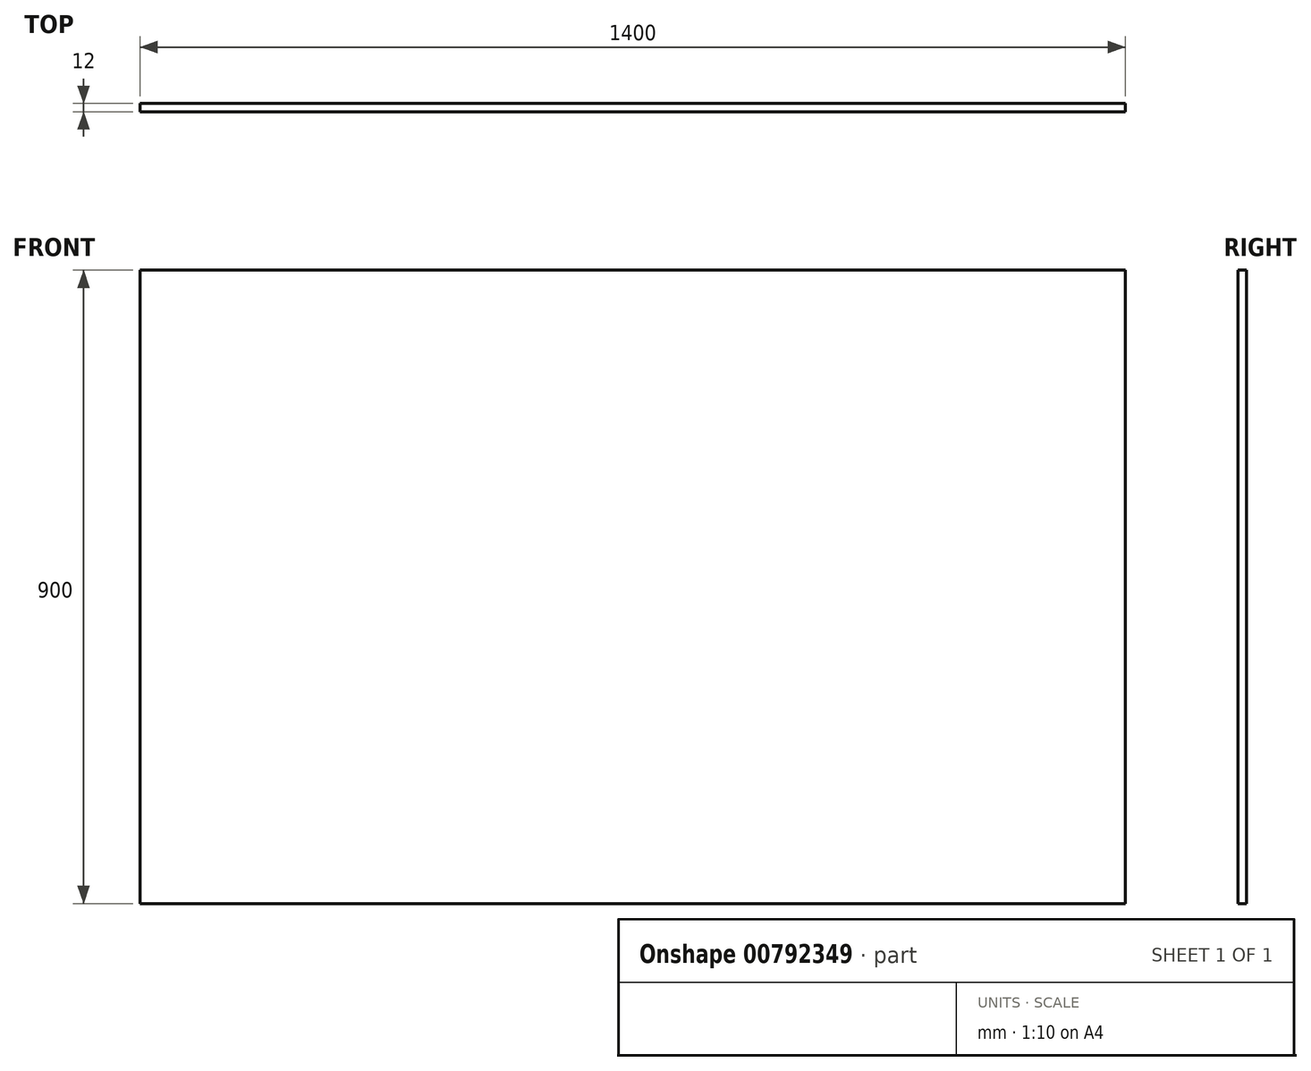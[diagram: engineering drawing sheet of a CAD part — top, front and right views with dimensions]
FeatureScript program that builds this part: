
annotation { "Feature Type Name" : "Feature", "Feature Type Description" : "" }
export const myFeature = defineFeature(function(context is Context, id is Id, definition is map)
    precondition{}
    {
        {
            var Q0;
            Q0=qCreatedBy(makeId("Front.planeOp"),FACE);
            var sketch = newSketch(context, id + "F0", { "sketchPlane" : qUnion([Q0])});
            skLineSegment(sketch, "E0.bottom", {"start": v(-700, 450) * mm, "end": v(700, 450) * mm});
            skLineSegment(sketch, "E0.top", {"start": v(-700, -450) * mm, "end": v(700, -450) * mm});
            skLineSegment(sketch, "E0.left", {"start": v(-700, 450) * mm, "end": v(-700, -450) * mm});
            skLineSegment(sketch, "E0.right", {"start": v(700, 450) * mm, "end": v(700, -450) * mm});
            skLineSegment(sketch, "E1", {"start": v(0, -450) * mm, "end": v(0, 450) * mm, "construction": true});
            skSolve(sketch);
        }
        {
            var Q0;
            Q0 = qSketchRegion(id + "F0", true);
            extrude(context, id + "F1", {"entities" : qUnion([Q0]), "depth" : 12 * mm, "offsetDistance" : 25 * mm});
        }
    });
